# Revit family: Chair-Soft_Seating-Allermuir-Haven-Corner_Unit-NoHeadrest-HAM201RH-RH
name_source: partatom
category: Furniture
revit_build: Autodesk Revit Architecture 2012 (Build: 20110916_2132)
units: mm (PartAtom-declared; Revit-internal decimal feet)

## types (1)
- HAM201RH
    04 CSI = 12 51 00
    95 CSI = 12510
    Assembly Code = E2020200
    Base = Metal - Allermuir - Black
    Brochure URL = http://www.allermuir.net
    Color Availability = See price list for material options
    Cushion = Fabric - Allermuir - Silcoates
    Default Elevation = 48"
    Depth = 31 1/2"
    Fabric Spec Sheets = http://www.allermuir.net
    Height = 25 77/128"
    LEED Stats URL = http://www.allermuir.net
    Manufacturer = Allermuir
    Manufacturer Fax = (419) 887 5805
    Model = HAM201RH
    Plugin Data URL = http://products.ecoscorecard.com
    Pricing URL = http://www.allermuir.net
    Product Line = Haven
    Product Page URL = http://www.allermuir.net
    Seat = Fabric - Allermuir - Silcoates
    Seat Height = 15 3/4"
    Spec Sheet URL = http://www.allermuir.net
    Subcategory = Soft Seating
    URL = http://www.allermuir.net
    Width = 69 11/32"
    ecoScorecard Product Page = http://products.ecoscorecard.com
    ecoScorecard_data = http://thesenatorgroup.ecoscorecard.com

## geometry (parser evidence)
native form markers: Blend x19, Sweep x5
no freeform markers — native parametric forms only
